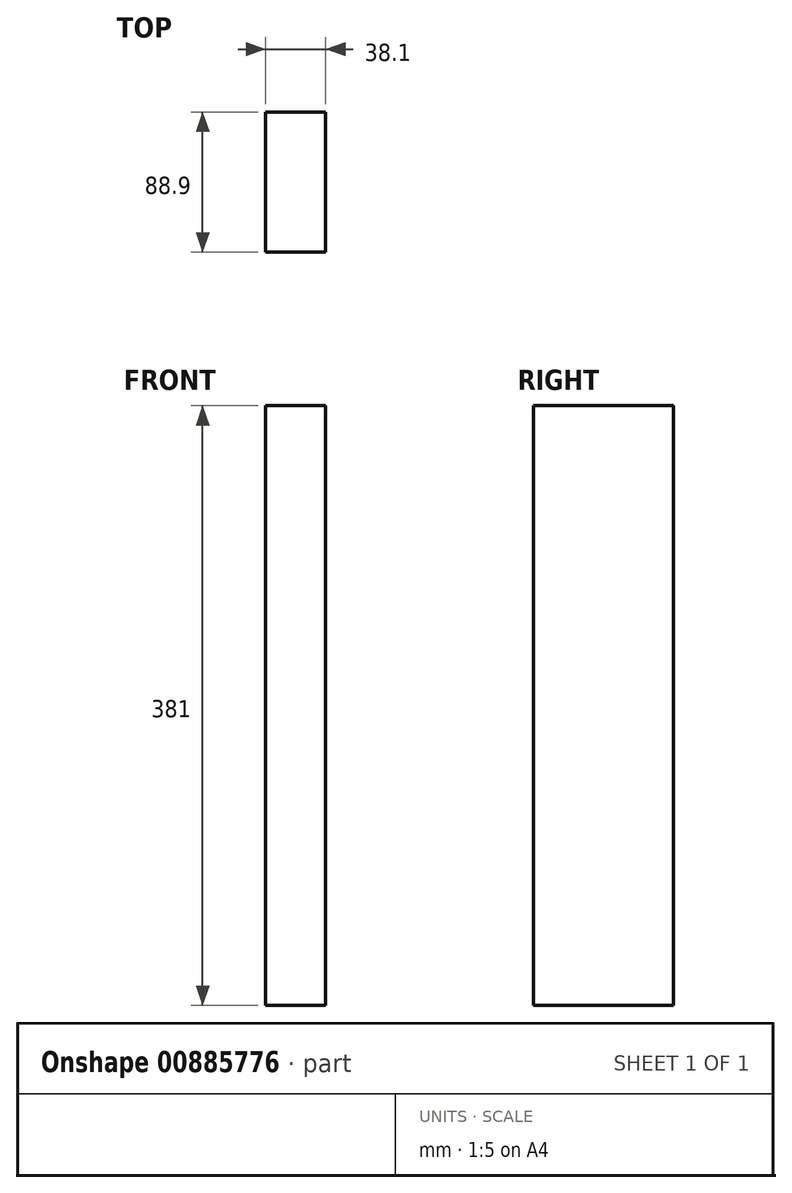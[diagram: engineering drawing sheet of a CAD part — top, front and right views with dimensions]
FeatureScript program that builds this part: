
annotation { "Feature Type Name" : "Feature", "Feature Type Description" : "" }
export const myFeature = defineFeature(function(context is Context, id is Id, definition is map)
    precondition{}
    {
        {
            var Q0;
            Q0=qCreatedBy(makeId("Top.planeOp"),FACE);
            var sketch = newSketch(context, id + "F0", { "sketchPlane" : qUnion([Q0])});
            skLineSegment(sketch, "E0.bottom", {"start": v(19.05, -44.45) * mm, "end": v(-19.05, -44.45) * mm});
            skLineSegment(sketch, "E0.top", {"start": v(19.05, 44.45) * mm, "end": v(-19.05, 44.45) * mm});
            skLineSegment(sketch, "E0.left", {"start": v(19.05, -44.45) * mm, "end": v(19.05, 44.45) * mm});
            skLineSegment(sketch, "E0.right", {"start": v(-19.05, -44.45) * mm, "end": v(-19.05, 44.45) * mm});
            skPoint(sketch, "E0.middle", {"position": v(0, 0) * mm});
            skSolve(sketch);
        }
        {
            var Q0;
            Q0=makeQuery(id+"F0.imprint","IMPRINT",FACE,{"disambiguationData":[TD([[makeQuery(id+"F0.imprint","IMPRINT",EDGE,{"derivedFrom":sQuery(id+"F0.wireOp",EDGE,"E0.bottom")}),-1.0]])]});
            extrude(context, id + "F1", {"entities" : qUnion([Q0]), "endBound" : BoundingType.SYMMETRIC, "depth" : 381 * mm, "offsetDistance" : 25.4 * mm});
        }
    });
